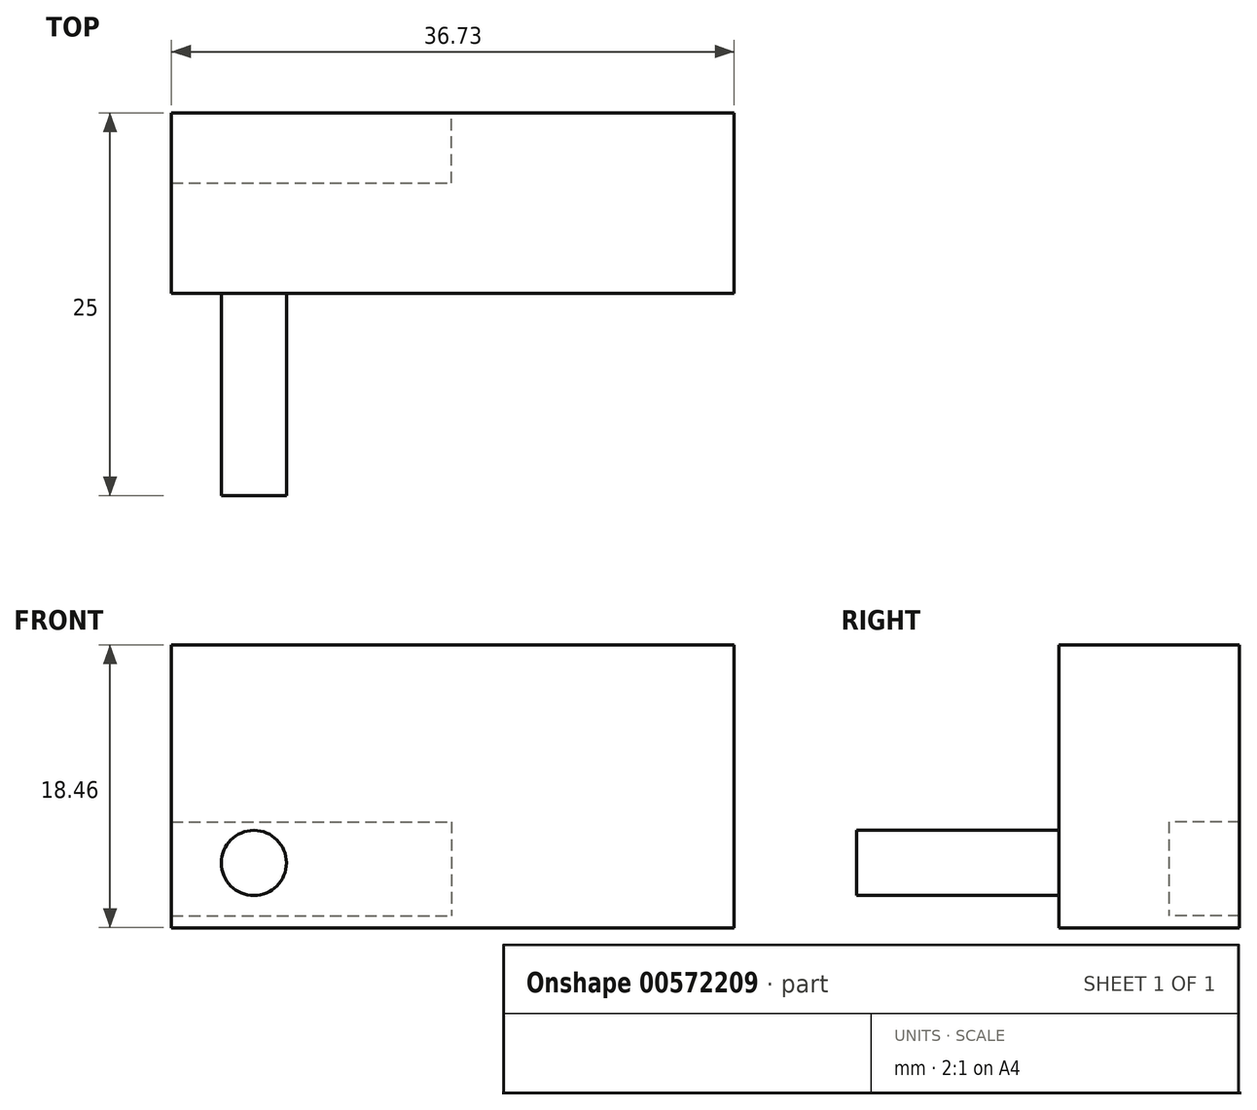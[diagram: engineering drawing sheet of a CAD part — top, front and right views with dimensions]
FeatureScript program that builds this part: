
annotation { "Feature Type Name" : "Feature", "Feature Type Description" : "" }
export const myFeature = defineFeature(function(context is Context, id is Id, definition is map)
    precondition{}
    {
        {
            var Q0;
            Q0=qCreatedBy(makeId("Front.planeOp"),FACE);
            var sketch = newSketch(context, id + "F0", { "sketchPlane" : qUnion([Q0])});
            skLineSegment(sketch, "E0.bottom", {"start": v(-18.27, 9.52) * mm, "end": v(18.46, 9.52) * mm});
            skLineSegment(sketch, "E0.top", {"start": v(-18.27, -8.94) * mm, "end": v(18.46, -8.94) * mm});
            skLineSegment(sketch, "E0.left", {"start": v(-18.27, 9.52) * mm, "end": v(-18.27, -8.94) * mm});
            skLineSegment(sketch, "E0.right", {"start": v(18.46, 9.52) * mm, "end": v(18.46, -8.94) * mm});
            skSolve(sketch);
        }
        {
            var Q0;
            Q0 = qSketchRegion(id + "F0", true);
            extrude(context, id + "F1", {"entities" : qUnion([Q0]), "depth" : 11.8 * mm, "offsetDistance" : 25 * mm});
        }
        {
            var Q0;
            Q0=qCreatedBy(makeId("Front.planeOp"),FACE);
            var sketch = newSketch(context, id + "F2", { "sketchPlane" : qUnion([Q0])});
            skCircle(sketch, "E1", {"center": v(-12.7, 4.33) * mm, "radius": 2.32 * mm});
            skCircle(sketch, "E2", {"center": v(-12.88, -4.71) * mm, "radius": 2.12 * mm});
            skSolve(sketch);
        }
        {
            var Q0;
            Q0=makeQuery(id+"F2.imprint","IMPRINT",FACE,{"disambiguationData":[TD([[makeQuery(id+"F2.imprint","IMPRINT",EDGE,{"derivedFrom":sQuery(id+"F2.wireOp",EDGE,"E2")}),1.0]])]});
            extrude(context, id + "F3", {"entities" : qUnion([Q0]), "operationType" : NewBodyOperationType.ADD, "depth" : 25 * mm, "offsetDistance" : 25 * mm});
        }
        {
            var Q0;
            Q0=qCreatedBy(makeId("Front.planeOp"),FACE);
            var sketch = newSketch(context, id + "F4", { "sketchPlane" : qUnion([Q0])});
            skLineSegment(sketch, "E3.bottom", {"start": v(-24.04, -2.02) * mm, "end": v(0, -2.02) * mm});
            skLineSegment(sketch, "E3.top", {"start": v(-24.04, -8.17) * mm, "end": v(0, -8.17) * mm});
            skLineSegment(sketch, "E3.left", {"start": v(-24.04, -2.02) * mm, "end": v(-24.04, -8.17) * mm});
            skLineSegment(sketch, "E3.right", {"start": v(0, -2.02) * mm, "end": v(0, -8.17) * mm});
            skSolve(sketch);
        }
        {
            var Q0;
            Q0 = qSketchRegion(id + "F4", true);
            extrude(context, id + "F5", {"entities" : qUnion([Q0]), "operationType" : NewBodyOperationType.REMOVE, "depth" : 4.6 * mm, "offsetDistance" : 25 * mm});
        }
    });
